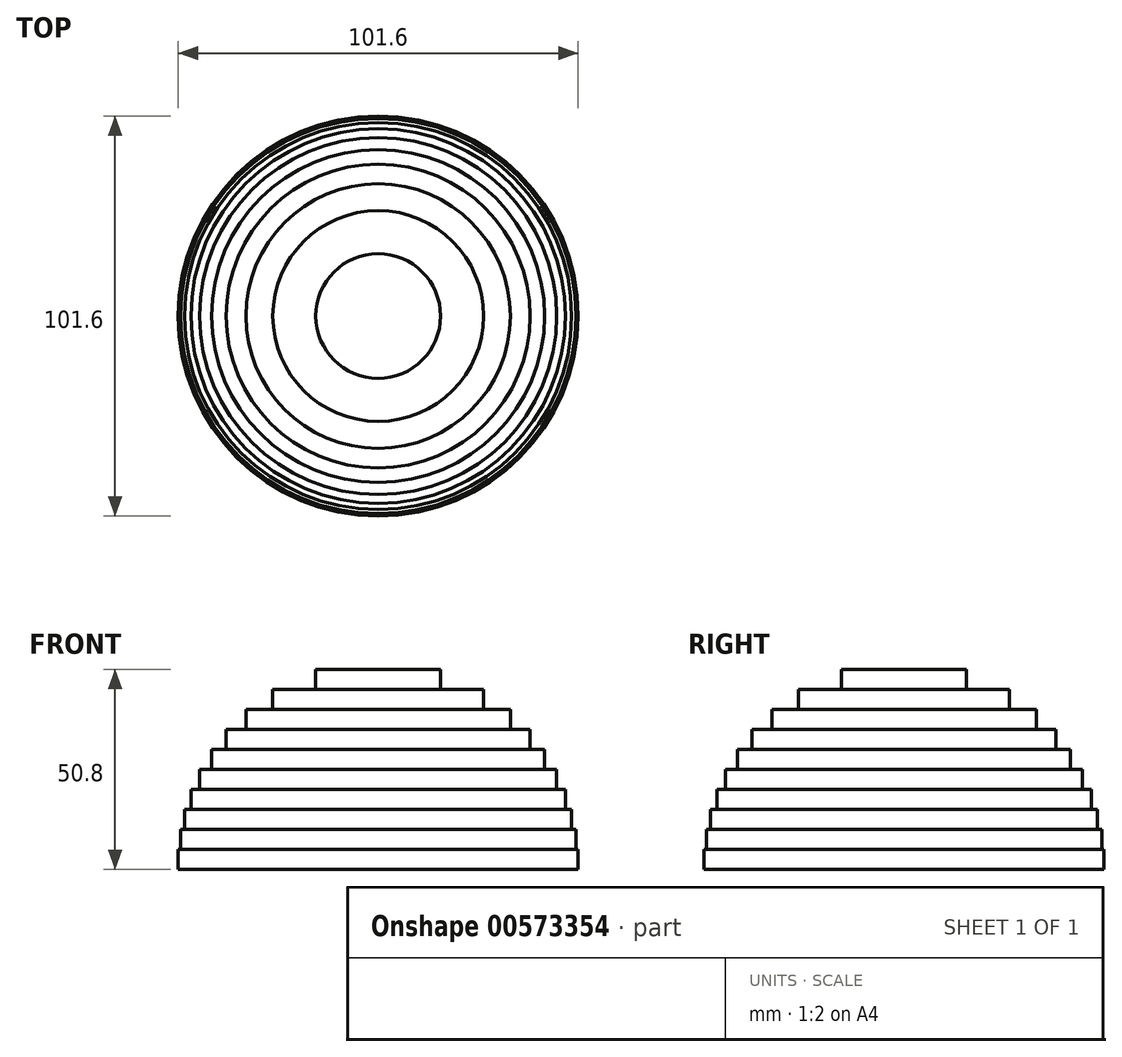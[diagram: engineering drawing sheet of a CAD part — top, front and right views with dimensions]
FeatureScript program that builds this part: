
annotation { "Feature Type Name" : "Feature", "Feature Type Description" : "" }
export const myFeature = defineFeature(function(context is Context, id is Id, definition is map)
    precondition{}
    {
        {
            var Q0;
            Q0=qCreatedBy(makeId("Top.planeOp"),FACE);
            var sketch = newSketch(context, id + "F0", { "sketchPlane" : qUnion([Q0])});
            skCircle(sketch, "E0", {"center": v(0, 0) * mm, "radius": 50.8 * mm});
            skSolve(sketch);
        }
        {
            var Q0;
            Q0 = qSketchRegion(id + "F0", true);
            extrude(context, id + "F1", {"entities" : qUnion([Q0]), "depth" : 5.08 * mm, "offsetDistance" : 25.4 * mm});
        }
        {
            var Q0;
            Q0=makeQuery(id+"F1.opExtrude","CAP_FACE",FACE,{"disambiguationData":[OSD([sQuery(id+"F0.wireOp",EDGE,"E0")])],"isStart":false});
            var sketch = newSketch(context, id + "F2", { "sketchPlane" : qUnion([Q0])});
            skCircle(sketch, "E1", {"center": v(0, 0) * mm, "radius": 50.22 * mm});
            skSolve(sketch);
        }
        {
            var Q0;
            Q0 = qSketchRegion(id + "F2", true);
            extrude(context, id + "F3", {"entities" : qUnion([Q0]), "operationType" : NewBodyOperationType.ADD, "depth" : 5.08 * mm, "offsetDistance" : 25.4 * mm});
        }
        {
            var Q0;
            Q0=makeQuery(id+"F3.opExtrude","CAP_FACE",FACE,{"disambiguationData":[OSD([sQuery(id+"F2.wireOp",EDGE,"E1")])],"isStart":false});
            var sketch = newSketch(context, id + "F4", { "sketchPlane" : qUnion([Q0])});
            skCircle(sketch, "E2", {"center": v(0, 0) * mm, "radius": 49.17 * mm});
            skSolve(sketch);
        }
        {
            var Q0;
            Q0 = qSketchRegion(id + "F4", true);
            extrude(context, id + "F5", {"entities" : qUnion([Q0]), "operationType" : NewBodyOperationType.ADD, "depth" : 5.08 * mm, "offsetDistance" : 25.4 * mm});
        }
        {
            var Q0;
            Q0=makeQuery(id+"F5.opExtrude","CAP_FACE",FACE,{"disambiguationData":[OSD([sQuery(id+"F4.wireOp",EDGE,"E2")])],"isStart":false});
            var sketch = newSketch(context, id + "F6", { "sketchPlane" : qUnion([Q0])});
            skCircle(sketch, "E3", {"center": v(0, 0) * mm, "radius": 47.57 * mm});
            skSolve(sketch);
        }
        {
            var Q0;
            Q0 = qSketchRegion(id + "F6", true);
            extrude(context, id + "F7", {"entities" : qUnion([Q0]), "operationType" : NewBodyOperationType.ADD, "depth" : 5.08 * mm, "offsetDistance" : 25.4 * mm});
        }
        {
            var Q0;
            Q0=makeQuery(id+"F7.opExtrude","CAP_FACE",FACE,{"disambiguationData":[OSD([sQuery(id+"F6.wireOp",EDGE,"E3")])],"isStart":false});
            var sketch = newSketch(context, id + "F8", { "sketchPlane" : qUnion([Q0])});
            skCircle(sketch, "E4", {"center": v(0, 0) * mm, "radius": 45.36 * mm});
            skSolve(sketch);
        }
        {
            var Q0;
            Q0 = qSketchRegion(id + "F8", true);
            extrude(context, id + "F9", {"entities" : qUnion([Q0]), "operationType" : NewBodyOperationType.ADD, "depth" : 5.08 * mm, "offsetDistance" : 25.4 * mm});
        }
        {
            var Q0;
            Q0=makeQuery(id+"F9.opExtrude","CAP_FACE",FACE,{"disambiguationData":[OSD([sQuery(id+"F8.wireOp",EDGE,"E4")])],"isStart":false});
            var sketch = newSketch(context, id + "F10", { "sketchPlane" : qUnion([Q0])});
            skCircle(sketch, "E5", {"center": v(0, 0) * mm, "radius": 42.3 * mm});
            skSolve(sketch);
        }
        {
            var Q0;
            Q0 = qSketchRegion(id + "F10", true);
            extrude(context, id + "F11", {"entities" : qUnion([Q0]), "operationType" : NewBodyOperationType.ADD, "depth" : 5.08 * mm, "offsetDistance" : 25.4 * mm});
        }
        {
            var Q0;
            Q0=makeQuery(id+"F11.opExtrude","CAP_FACE",FACE,{"disambiguationData":[OSD([sQuery(id+"F10.wireOp",EDGE,"E5")])],"isStart":false});
            var sketch = newSketch(context, id + "F12", { "sketchPlane" : qUnion([Q0])});
            skCircle(sketch, "E6", {"center": v(0, 0) * mm, "radius": 38.6 * mm});
            skSolve(sketch);
        }
        {
            var Q0;
            Q0 = qSketchRegion(id + "F12", true);
            extrude(context, id + "F13", {"entities" : qUnion([Q0]), "operationType" : NewBodyOperationType.ADD, "depth" : 5.08 * mm, "offsetDistance" : 25.4 * mm});
        }
        {
            var Q0;
            Q0=makeQuery(id+"F13.opExtrude","CAP_FACE",FACE,{"disambiguationData":[OSD([sQuery(id+"F12.wireOp",EDGE,"E6")])],"isStart":false});
            var sketch = newSketch(context, id + "F14", { "sketchPlane" : qUnion([Q0])});
            skCircle(sketch, "E7", {"center": v(0, 0) * mm, "radius": 33.6 * mm});
            skSolve(sketch);
        }
        {
            var Q0;
            Q0 = qSketchRegion(id + "F14", true);
            extrude(context, id + "F15", {"entities" : qUnion([Q0]), "operationType" : NewBodyOperationType.ADD, "depth" : 5.08 * mm, "offsetDistance" : 25.4 * mm});
        }
        {
            var Q0;
            Q0=makeQuery(id+"F15.opExtrude","CAP_FACE",FACE,{"disambiguationData":[OSD([sQuery(id+"F14.wireOp",EDGE,"E7")])],"isStart":false});
            var sketch = newSketch(context, id + "F16", { "sketchPlane" : qUnion([Q0])});
            skCircle(sketch, "E8", {"center": v(0, 0) * mm, "radius": 26.77 * mm});
            skSolve(sketch);
        }
        {
            var Q0;
            Q0 = qSketchRegion(id + "F16", true);
            extrude(context, id + "F17", {"entities" : qUnion([Q0]), "operationType" : NewBodyOperationType.ADD, "depth" : 5.08 * mm, "offsetDistance" : 25.4 * mm});
        }
        {
            var Q0;
            Q0=makeQuery(id+"F17.opExtrude","CAP_FACE",FACE,{"disambiguationData":[OSD([sQuery(id+"F16.wireOp",EDGE,"E8")])],"isStart":false});
            var sketch = newSketch(context, id + "F18", { "sketchPlane" : qUnion([Q0])});
            skCircle(sketch, "E9", {"center": v(0, 0) * mm, "radius": 15.85 * mm});
            skSolve(sketch);
        }
        {
            var Q0;
            Q0 = qSketchRegion(id + "F18", true);
            extrude(context, id + "F19", {"entities" : qUnion([Q0]), "operationType" : NewBodyOperationType.ADD, "depth" : 5.08 * mm, "offsetDistance" : 25.4 * mm});
        }
    });
